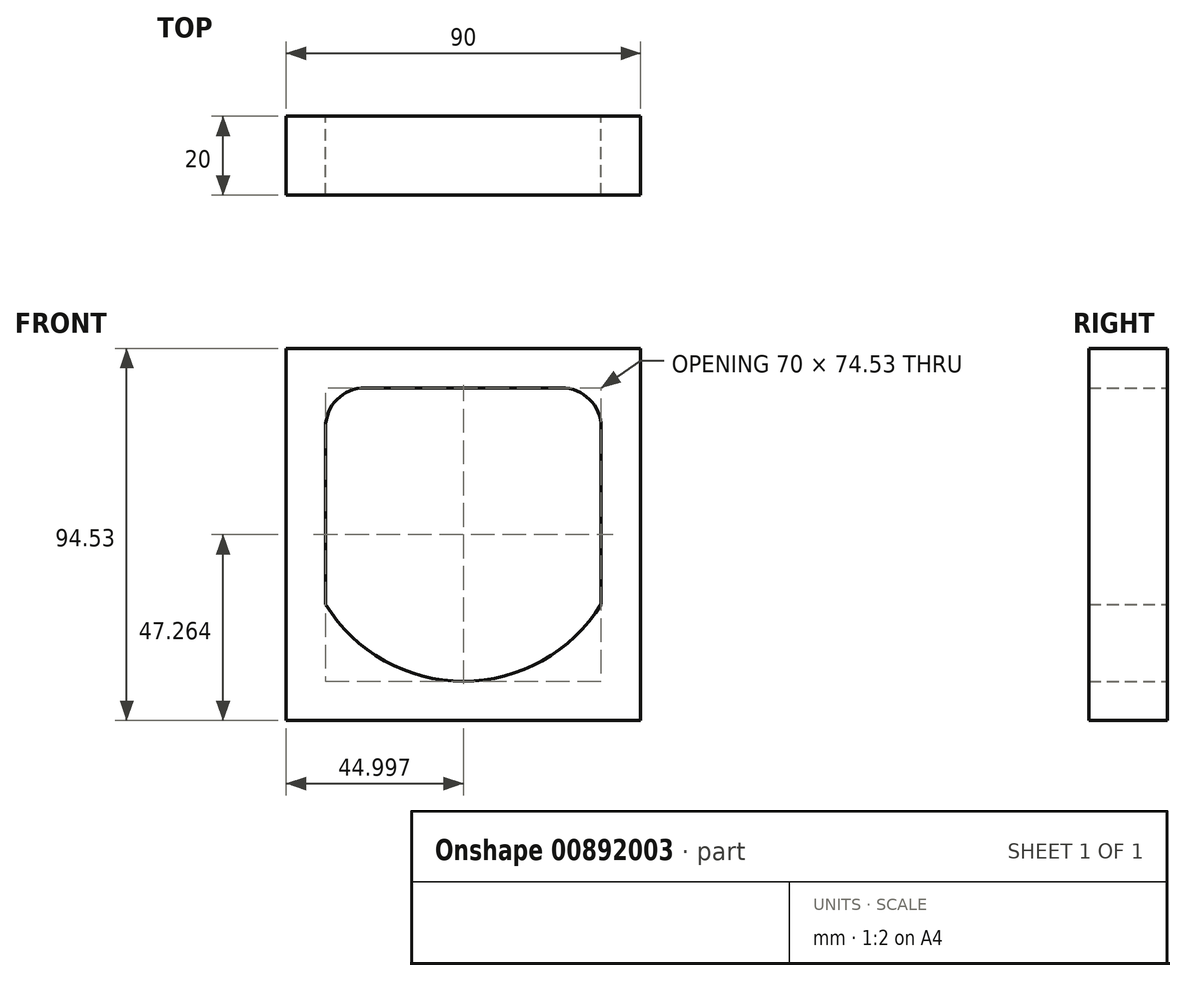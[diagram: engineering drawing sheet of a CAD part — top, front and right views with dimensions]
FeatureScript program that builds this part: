
annotation { "Feature Type Name" : "Feature", "Feature Type Description" : "" }
export const myFeature = defineFeature(function(context is Context, id is Id, definition is map)
    precondition{}
    {
        {
            var Q0;
            Q0=qCreatedBy(makeId("Front.planeOp"),FACE);
            var sketch = newSketch(context, id + "F0", { "sketchPlane" : qUnion([Q0])});
            skLineSegment(sketch, "E0.bottom", {"start": v(-14.68, 26.24) * mm, "end": v(35.32, 26.24) * mm});
            skLineSegment(sketch, "E0.left", {"start": v(-24.68, 16.24) * mm, "end": v(-24.68, -28.76) * mm});
            skLineSegment(sketch, "E0.right", {"start": v(45.32, 16.24) * mm, "end": v(45.32, -28.76) * mm});
            skLineSegment(sketch, "E1", {"start": v(10.32, -48.29) * mm, "end": v(10.32, 26.24) * mm, "construction": true});
            skLineSegment(sketch, "E2", {"start": v(-24.68, -28.76) * mm, "end": v(45.32, -28.76) * mm, "construction": true});
            skPoint(sketch, "E3.orphan", {"position": v(45.32, -48.29) * mm});
            skPoint(sketch, "E4.orphan", {"position": v(-24.68, -48.29) * mm});
            skArc(sketch, "E5", {"start": v(-24.68, -28.76) * mm, "mid": v(10.32, -48.29) * mm, "end": v(45.32, -28.76) * mm});
            skPoint(sketch, "E6.visualSharp", {"position": v(-24.68, 26.24) * mm});
            skArc(sketch, "E6.filletArc", {"start": v(-14.68, 26.24) * mm, "mid": v(-21.75, 23.3) * mm, "end": v(-24.68, 16.24) * mm});
            skPoint(sketch, "E7.visualSharp", {"position": v(45.32, 26.24) * mm});
            skArc(sketch, "E7.filletArc", {"start": v(45.32, 16.24) * mm, "mid": v(42.39, 23.3) * mm, "end": v(35.32, 26.24) * mm});
            skLineSegment(sketch, "E8.bottom", {"start": v(-34.68, 36.24) * mm, "end": v(55.32, 36.24) * mm});
            skLineSegment(sketch, "E8.top", {"start": v(-34.68, -58.29) * mm, "end": v(55.32, -58.29) * mm});
            skLineSegment(sketch, "E8.left", {"start": v(-34.68, 36.24) * mm, "end": v(-34.68, -58.29) * mm});
            skLineSegment(sketch, "E8.right", {"start": v(55.32, 36.24) * mm, "end": v(55.32, -58.29) * mm});
            skSolve(sketch);
        }
        {
            var Q0;
            Q0=makeQuery(id+"F0.imprint","IMPRINT",FACE,{"disambiguationData":[TD([[makeQuery(id+"F0.imprint","IMPRINT",EDGE,{"derivedFrom":sQuery(id+"F0.wireOp",EDGE,"E0.bottom")}),1.0]])]});
            extrude(context, id + "F1", {"entities" : qUnion([Q0]), "depth" : 20 * mm, "offsetDistance" : 25 * mm});
        }
    });
